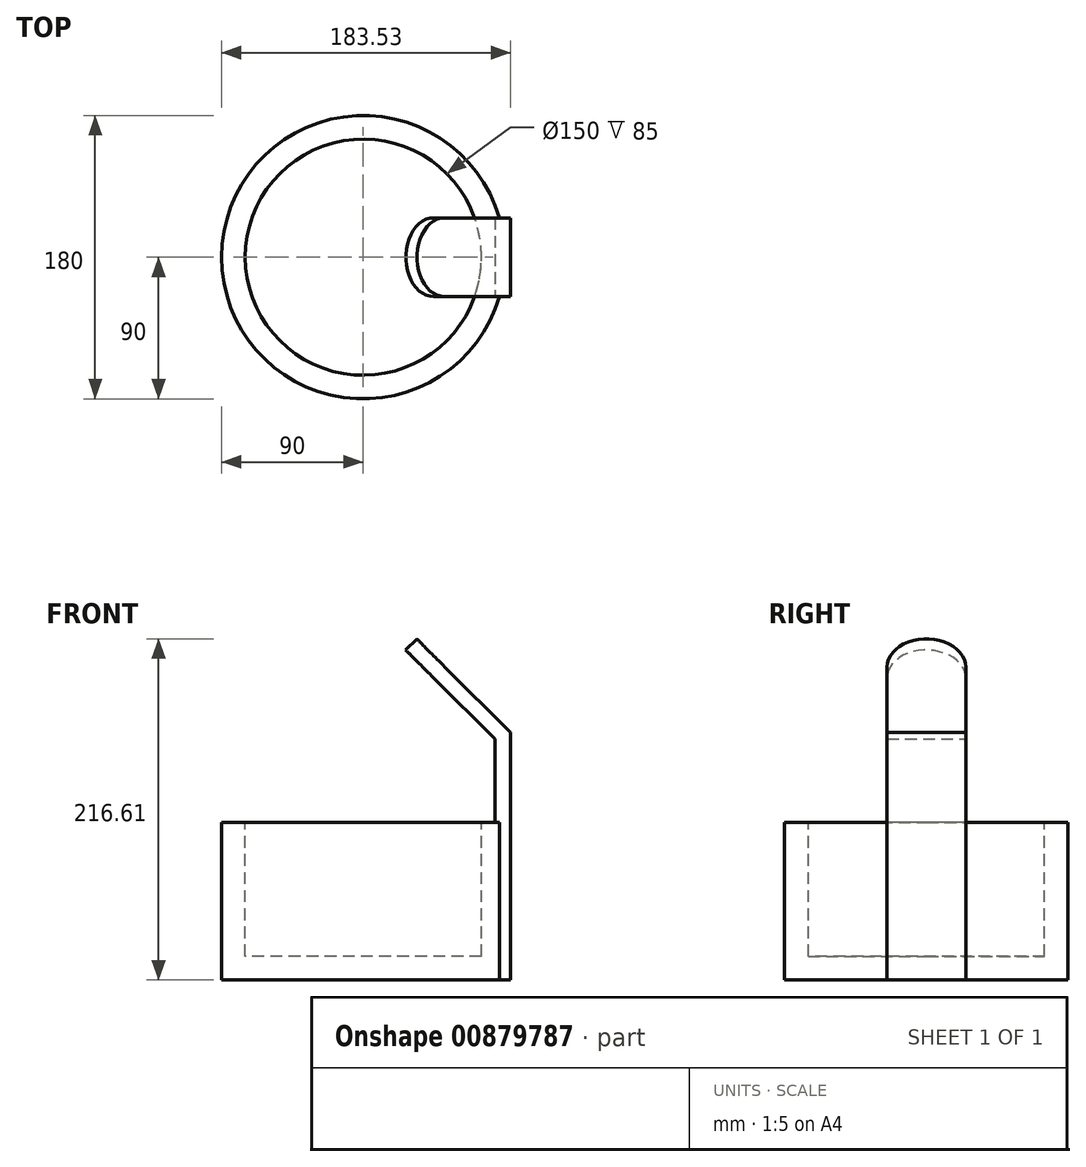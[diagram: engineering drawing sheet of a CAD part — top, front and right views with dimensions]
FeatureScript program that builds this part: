
annotation { "Feature Type Name" : "Feature", "Feature Type Description" : "" }
export const myFeature = defineFeature(function(context is Context, id is Id, definition is map)
    precondition{}
    {
        {
            var Q0;
            Q0=qCreatedBy(makeId("Front.planeOp"),FACE);
            var sketch = newSketch(context, id + "F0", { "sketchPlane" : qUnion([Q0])});
            skLineSegment(sketch, "E0", {"start": v(0, -25.52) * mm, "end": v(0, -40.52) * mm});
            skLineSegment(sketch, "E1", {"start": v(0, -40.52) * mm, "end": v(90, -40.52) * mm});
            skLineSegment(sketch, "E2", {"start": v(90, -40.52) * mm, "end": v(90, 59.48) * mm});
            skLineSegment(sketch, "E3", {"start": v(90, 59.48) * mm, "end": v(75, 59.48) * mm});
            skLineSegment(sketch, "E4", {"start": v(75, 59.48) * mm, "end": v(75, -25.52) * mm});
            skLineSegment(sketch, "E5", {"start": v(75, -25.52) * mm, "end": v(0, -25.52) * mm});
            skSolve(sketch);
        }
        {
            var Q0;
            Q0 = qSketchRegion(id + "F0", true);
            var Q1;
            Q1=sQuery(id+"F0.wireOp",EDGE,"E0");
            revolve(context, id + "F1", {"surfaceOperationType" : NewSurfaceOperationType.NEW, "entities" : qUnion([Q0]), "axis" : qUnion([Q1]), "revolveType" : RevolveType.FULL});
        }
        {
            var Q0;
            Q0=qCreatedBy(makeId("Front.planeOp"),FACE);
            var sketch = newSketch(context, id + "F2", { "sketchPlane" : qUnion([Q0])});
            skLineSegment(sketch, "E6", {"start": v(93.53, -40.52) * mm, "end": v(93.53, 116.6) * mm});
            skLineSegment(sketch, "E7", {"start": v(93.53, 116.6) * mm, "end": v(34.04, 176.1) * mm});
            skLineSegment(sketch, "E8", {"start": v(34.04, 176.1) * mm, "end": v(26.97, 169.02) * mm});
            skLineSegment(sketch, "E9", {"start": v(26.97, 169.02) * mm, "end": v(83.53, 112.45) * mm});
            skLineSegment(sketch, "E10", {"start": v(83.53, 112.45) * mm, "end": v(83.53, -40.52) * mm});
            skLineSegment(sketch, "E11", {"start": v(83.53, -40.52) * mm, "end": v(93.53, -40.52) * mm});
            skSolve(sketch);
        }
        {
            var Q0;
            Q0 = qSketchRegion(id + "F2", true);
            extrude(context, id + "F3", {"entities" : qUnion([Q0]), "operationType" : NewBodyOperationType.ADD, "endBound" : BoundingType.SYMMETRIC, "depth" : 50 * mm, "offsetDistance" : 25 * mm});
        }
        {
            var Q0;
            Q0=makeQuery(id+"F3.opExtrude","CAP_EDGE",EDGE,{"disambiguationData":[OSD([sQuery(id+"F2.wireOp",EDGE,"E8")])],"isStart":false});
            var Q1;
            Q1=makeQuery(id+"F3.opExtrude","CAP_EDGE",EDGE,{"disambiguationData":[OSD([sQuery(id+"F2.wireOp",EDGE,"E8")])],"isStart":true});
            fillet(context, id + "F4", {"entities" : qUnion([Q0, Q1]), "radius" : 25 * mm, "tangentPropagation" : true, "allowEdgeOverflow" : false});
        }
    });
